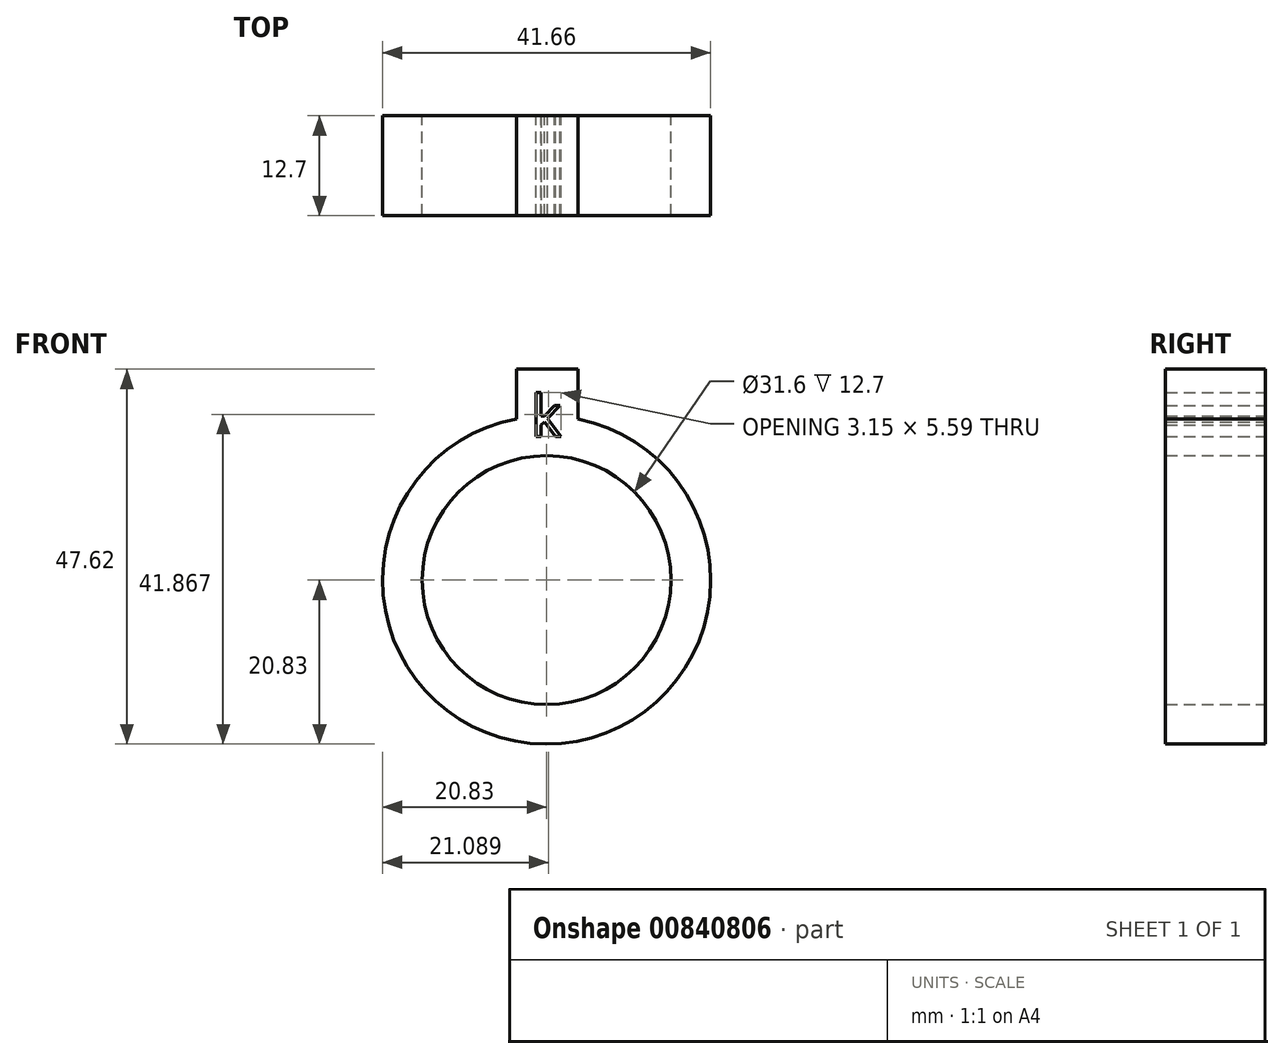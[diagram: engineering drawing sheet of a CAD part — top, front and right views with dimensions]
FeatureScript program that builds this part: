
annotation { "Feature Type Name" : "Feature", "Feature Type Description" : "" }
export const myFeature = defineFeature(function(context is Context, id is Id, definition is map)
    precondition{}
    {
        {
            var Q0;
            Q0=qCreatedBy(makeId("Front.planeOp"),FACE);
            var sketch = newSketch(context, id + "F0", { "sketchPlane" : qUnion([Q0])});
            skCircle(sketch, "E0", {"center": v(0, 0) * mm, "radius": 15.8 * mm});
            skCircle(sketch, "E1", {"center": v(0, 0) * mm, "radius": 20.83 * mm});
            skLineSegment(sketch, "E2", {"start": v(4, 15.29) * mm, "end": v(4, 26.79) * mm});
            skLineSegment(sketch, "E3", {"start": v(4, 26.79) * mm, "end": v(-3.82, 26.79) * mm});
            skLineSegment(sketch, "E4", {"start": v(-3.82, 26.79) * mm, "end": v(-3.82, 15.33) * mm});
            skLineSegment(sketch, "E5", {"start": v(-3.82, 15.33) * mm, "end": v(4, 15.29) * mm});
            skText(sketch, "E6", { "text": "k", "fontName": "OpenSans-Regular.ttf"});
            const initialGuessF0  = {"E6": [-0.00195, 0.01824, 1, 0, 0.0053]};
            skSetInitialGuess(sketch, initialGuessF0);
            skSolve(sketch);
        }
        {
            var Q0;
            Q0 = qSketchRegion(id + "F0", true);
            extrude(context, id + "F1", {"entities" : qUnion([Q0]), "depth" : 10.16 * mm, "offsetDistance" : 25.4 * mm});
        }
        {
            var Q0;
            Q0 = qSketchRegion(id + "F0", true);
            extrude(context, id + "F2", {"entities" : qUnion([Q0]), "operationType" : NewBodyOperationType.ADD, "depth" : 12.7 * mm, "offsetDistance" : 25.4 * mm});
        }
    });
